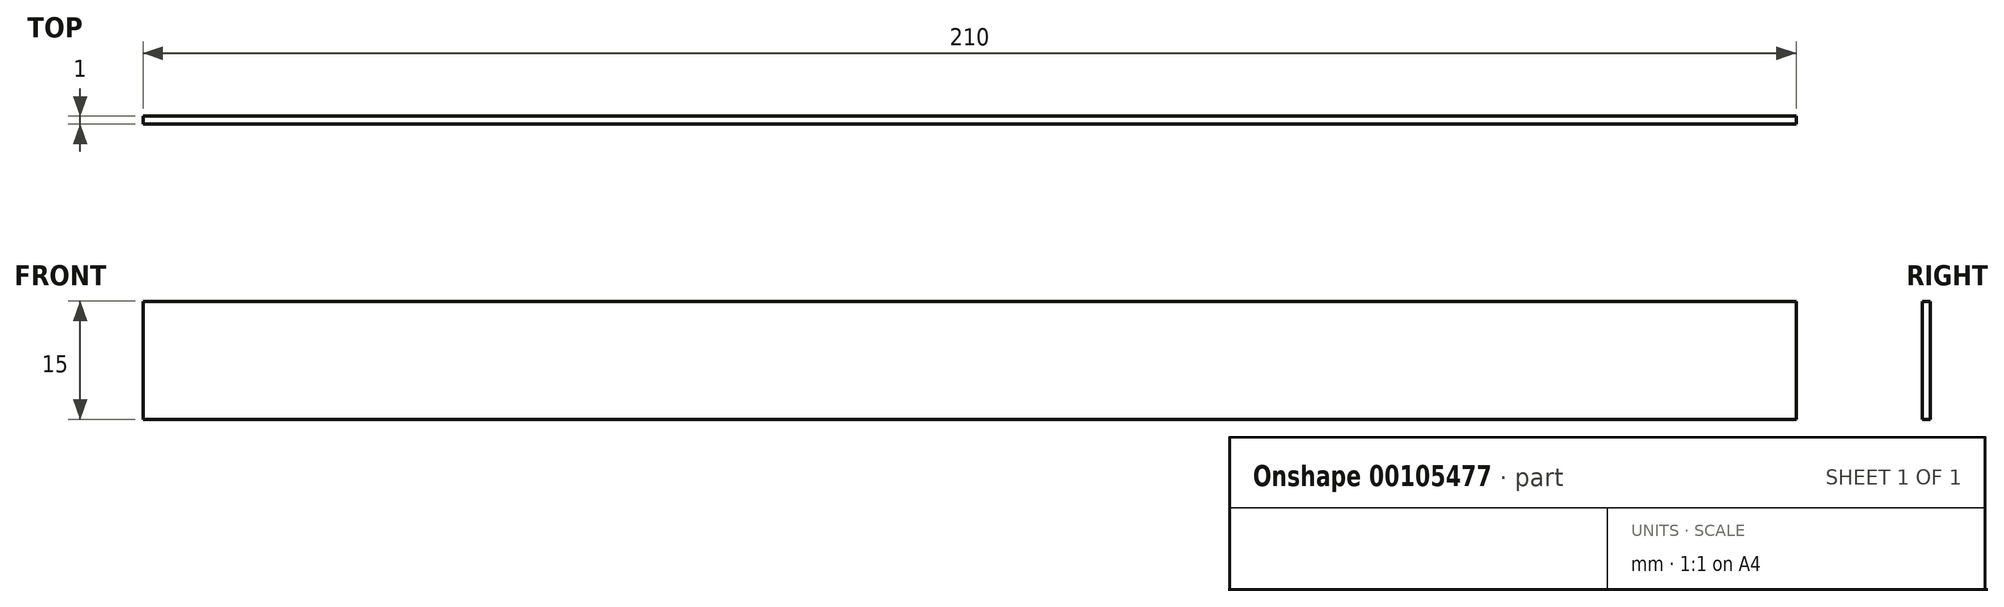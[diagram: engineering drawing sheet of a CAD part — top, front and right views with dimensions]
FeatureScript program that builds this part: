
annotation { "Feature Type Name" : "Feature", "Feature Type Description" : "" }
export const myFeature = defineFeature(function(context is Context, id is Id, definition is map)
    precondition{}
    {
        {
            var Q0;
            Q0=qCreatedBy(makeId("Front.planeOp"),FACE);
            var sketch = newSketch(context, id + "F0", { "sketchPlane" : qUnion([Q0])});
            skLineSegment(sketch, "E0.bottom", {"start": v(109.69, -16.8) * mm, "end": v(-100.31, -16.8) * mm});
            skLineSegment(sketch, "E0.top", {"start": v(109.69, -1.8) * mm, "end": v(-100.31, -1.8) * mm});
            skLineSegment(sketch, "E0.left", {"start": v(109.69, -16.8) * mm, "end": v(109.69, -1.8) * mm});
            skLineSegment(sketch, "E0.right", {"start": v(-100.31, -16.8) * mm, "end": v(-100.31, -1.8) * mm});
            skPoint(sketch, "E0.middle", {"position": v(4.69, -9.3) * mm});
            skSolve(sketch);
        }
        {
            var Q0;
            Q0=makeQuery(id+"F0.imprint","IMPRINT",FACE,{"disambiguationData":[TD([[makeQuery(id+"F0.imprint","IMPRINT",EDGE,{"derivedFrom":sQuery(id+"F0.wireOp",EDGE,"E0.bottom")}),-1.0]])]});
            extrude(context, id + "F1", {"entities" : qUnion([Q0]), "depth" : 1 * mm});
        }
    });
